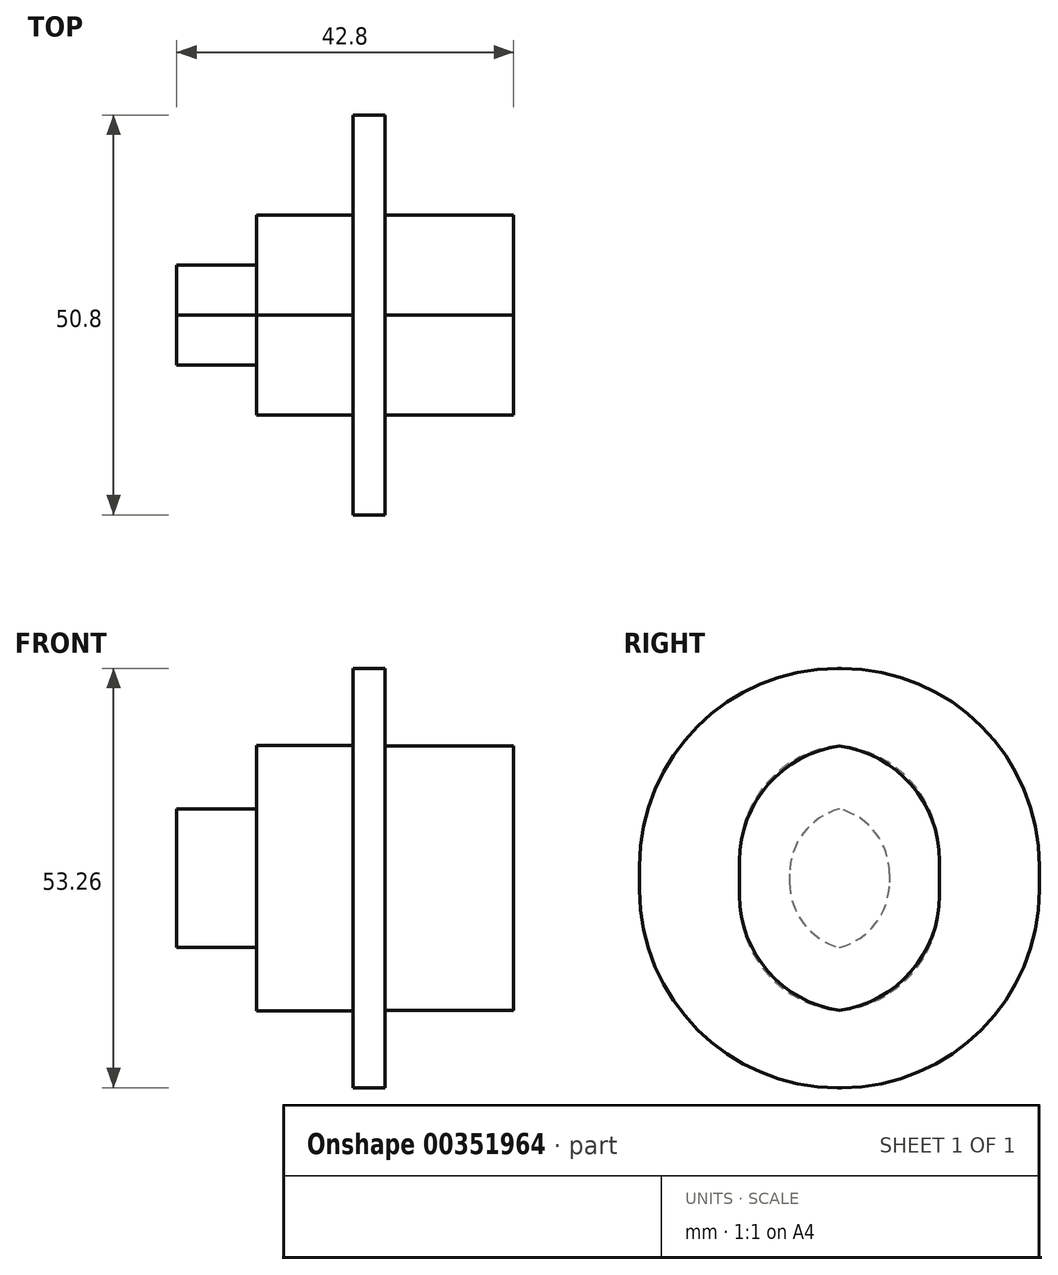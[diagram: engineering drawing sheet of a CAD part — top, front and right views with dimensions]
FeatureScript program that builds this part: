
annotation { "Feature Type Name" : "Feature", "Feature Type Description" : "" }
export const myFeature = defineFeature(function(context is Context, id is Id, definition is map)
    precondition{}
    {
        {
            var Q0;
            Q0=qCreatedBy(makeId("Front.planeOp"),FACE);
            var sketch = newSketch(context, id + "F0", { "sketchPlane" : qUnion([Q0])});
            skLineSegment(sketch, "E0.top", {"start": v(-32.63, 9.04) * mm, "end": v(-42.8, 9.04) * mm});
            skLineSegment(sketch, "E0.left", {"start": v(0, 0) * mm, "end": v(0, 9.04) * mm});
            skLineSegment(sketch, "E0.right", {"start": v(-42.8, 0) * mm, "end": v(-42.8, 9.04) * mm});
            skLineSegment(sketch, "E1.top", {"start": v(0, 16.87) * mm, "end": v(-16.32, 16.87) * mm});
            skLineSegment(sketch, "E1.left", {"start": v(0, 9.04) * mm, "end": v(0, 16.87) * mm});
            skLineSegment(sketch, "E1.right", {"start": v(-32.63, 9.04) * mm, "end": v(-32.63, 16.87) * mm});
            skLineSegment(sketch, "E2.top", {"start": v(-16.32, 26.6) * mm, "end": v(-20.42, 26.6) * mm});
            skLineSegment(sketch, "E2.left", {"start": v(-16.32, 16.87) * mm, "end": v(-16.32, 26.6) * mm});
            skLineSegment(sketch, "E2.right", {"start": v(-20.42, 16.87) * mm, "end": v(-20.42, 26.6) * mm});
            skLineSegment(sketch, "E3.trimOffspring", {"start": v(-20.42, 16.87) * mm, "end": v(-32.63, 16.87) * mm});
            skPoint(sketch, "E4.right.end.orphan", {"position": v(0, -9.18) * mm});
            skLineSegment(sketch, "E5.top", {"start": v(-42.8, -9.18) * mm, "end": v(-32.63, -9.18) * mm});
            skLineSegment(sketch, "E5.left", {"start": v(-42.8, 0) * mm, "end": v(-42.8, -9.18) * mm});
            skLineSegment(sketch, "E5.right", {"start": v(0, 0) * mm, "end": v(0, -9.18) * mm});
            skLineSegment(sketch, "E6.top", {"start": v(-32.63, -16.98) * mm, "end": v(-20.42, -16.98) * mm});
            skLineSegment(sketch, "E6.left", {"start": v(-32.63, -9.18) * mm, "end": v(-32.63, -16.98) * mm});
            skLineSegment(sketch, "E6.right", {"start": v(0, -9.18) * mm, "end": v(0, -16.98) * mm});
            skLineSegment(sketch, "E7.top", {"start": v(-20.42, -26.67) * mm, "end": v(-16.32, -26.67) * mm});
            skLineSegment(sketch, "E7.left", {"start": v(-20.42, -16.98) * mm, "end": v(-20.42, -26.67) * mm});
            skLineSegment(sketch, "E7.right", {"start": v(-16.32, -16.98) * mm, "end": v(-16.32, -26.67) * mm});
            skLineSegment(sketch, "E8.trimOffspring", {"start": v(-16.32, -16.98) * mm, "end": v(0, -16.98) * mm});
            skLineSegment(sketch, "E9", {"start": v(-20.42, 16.87) * mm, "end": v(-20.42, -16.98) * mm});
            skLineSegment(sketch, "E10", {"start": v(-16.32, -16.98) * mm, "end": v(-16.32, 16.87) * mm});
            skLineSegment(sketch, "E11", {"start": v(-32.63, 9.04) * mm, "end": v(-32.63, -9.18) * mm});
            skSolve(sketch);
        }
        {
            var Q0;
            Q0=makeQuery(id+"F0.imprint","IMPRINT",FACE,{"disambiguationData":[TD([[makeQuery(id+"F0.imprint","IMPRINT",EDGE,{"derivedFrom":sQuery(id+"F0.wireOp",EDGE,"E2.top")}),1.0]])]});
            extrude(context, id + "F1", {"entities" : qUnion([Q0]), "endBound" : BoundingType.SYMMETRIC, "oppositeDirection" : true, "depth" : 50.8 * mm});
        }
        {
            var Q0;
            Q0=makeQuery(id+"F0.imprint","IMPRINT",FACE,{"disambiguationData":[TD([[makeQuery(id+"F0.imprint","IMPRINT",EDGE,{"derivedFrom":sQuery(id+"F0.wireOp",EDGE,"E1.right")}),-1.0]])]});
            var Q1;
            Q1=makeQuery(id+"F0.imprint","IMPRINT",FACE,{"disambiguationData":[TD([[makeQuery(id+"F0.imprint","IMPRINT",EDGE,{"derivedFrom":sQuery(id+"F0.wireOp",EDGE,"E0.left")}),1.0]])]});
            extrude(context, id + "F2", {"entities" : qUnion([Q0, Q1]), "operationType" : NewBodyOperationType.ADD, "endBound" : BoundingType.SYMMETRIC, "depth" : 25.4 * mm});
        }
        {
            var Q0;
            Q0=makeQuery(id+"F0.imprint","IMPRINT",FACE,{"disambiguationData":[TD([[makeQuery(id+"F0.imprint","IMPRINT",EDGE,{"derivedFrom":sQuery(id+"F0.wireOp",EDGE,"E0.top")}),1.0]])]});
            extrude(context, id + "F3", {"entities" : qUnion([Q0]), "operationType" : NewBodyOperationType.ADD, "endBound" : BoundingType.SYMMETRIC, "depth" : 12.7 * mm});
        }
        {
            var Q0;
            Q0=makeQuery(id+"F3.opExtrude","CAP_EDGE",EDGE,{"disambiguationData":[OSD([sQuery(id+"F0.wireOp",EDGE,"E0.top")])],"isStart":false});
            var Q1;
            Q1=makeQuery(id+"F3.opExtrude","CAP_EDGE",EDGE,{"disambiguationData":[OSD([sQuery(id+"F0.wireOp",EDGE,"E5.top")])],"isStart":false});
            var Q2;
            Q2=makeQuery(id+"F3.opExtrude","CAP_EDGE",EDGE,{"disambiguationData":[OSD([sQuery(id+"F0.wireOp",EDGE,"E0.top")])],"isStart":true});
            var Q3;
            Q3=makeQuery(id+"F3.opExtrude","CAP_EDGE",EDGE,{"disambiguationData":[OSD([sQuery(id+"F0.wireOp",EDGE,"E5.top")])],"isStart":true});
            fillet(context, id + "F4", {"entities" : qUnion([Q0, Q1, Q2, Q3]), "radius" : 8.58 * mm, "tangentPropagation" : true, "allowEdgeOverflow" : false});
        }
        {
            var Q0;
            Q0=makeQuery(id+"F2.opExtrude","CAP_EDGE",EDGE,{"disambiguationData":[OSD([sQuery(id+"F0.wireOp",EDGE,"E3.trimOffspring")])],"isStart":true});
            var Q1;
            Q1=makeQuery(id+"F2.opExtrude","CAP_EDGE",EDGE,{"disambiguationData":[OSD([sQuery(id+"F0.wireOp",EDGE,"E6.top")])],"isStart":true});
            var Q2;
            Q2=makeQuery(id+"F2.opExtrude","CAP_EDGE",EDGE,{"disambiguationData":[OSD([sQuery(id+"F0.wireOp",EDGE,"E3.trimOffspring")])],"isStart":false});
            var Q3;
            Q3=makeQuery(id+"F2.opExtrude","CAP_EDGE",EDGE,{"disambiguationData":[OSD([sQuery(id+"F0.wireOp",EDGE,"E6.top")])],"isStart":false});
            fillet(context, id + "F5", {"entities" : qUnion([Q0, Q1, Q2, Q3]), "radius" : 14.1 * mm, "tangentPropagation" : true, "allowEdgeOverflow" : false});
        }
        {
            var Q0;
            Q0=makeQuery(id+"F1.opExtrude","CAP_EDGE",EDGE,{"disambiguationData":[OSD([sQuery(id+"F0.wireOp",EDGE,"E2.top")])],"isStart":true});
            var Q1;
            Q1=makeQuery(id+"F1.opExtrude","CAP_EDGE",EDGE,{"disambiguationData":[OSD([sQuery(id+"F0.wireOp",EDGE,"E7.top")])],"isStart":true});
            var Q2;
            Q2=makeQuery(id+"F1.opExtrude","CAP_EDGE",EDGE,{"disambiguationData":[OSD([sQuery(id+"F0.wireOp",EDGE,"E2.top")])],"isStart":false});
            var Q3;
            Q3=makeQuery(id+"F1.opExtrude","CAP_EDGE",EDGE,{"disambiguationData":[OSD([sQuery(id+"F0.wireOp",EDGE,"E7.top")])],"isStart":false});
            fillet(context, id + "F6", {"entities" : qUnion([Q0, Q1, Q2, Q3]), "radius" : 25.14 * mm, "tangentPropagation" : true, "allowEdgeOverflow" : false});
        }
        {
            var Q0;
            Q0=makeQuery(id+"F2.opExtrude","CAP_EDGE",EDGE,{"disambiguationData":[OSD([sQuery(id+"F0.wireOp",EDGE,"E1.top")])],"isStart":true});
            var Q1;
            Q1=makeQuery(id+"F2.opExtrude","CAP_EDGE",EDGE,{"disambiguationData":[OSD([sQuery(id+"F0.wireOp",EDGE,"E8.trimOffspring")])],"isStart":true});
            var Q2;
            Q2=makeQuery(id+"F2.opExtrude","CAP_EDGE",EDGE,{"disambiguationData":[OSD([sQuery(id+"F0.wireOp",EDGE,"E1.top")])],"isStart":false});
            var Q3;
            Q3=makeQuery(id+"F2.opExtrude","CAP_EDGE",EDGE,{"disambiguationData":[OSD([sQuery(id+"F0.wireOp",EDGE,"E8.trimOffspring")])],"isStart":false});
            fillet(context, id + "F7", {"entities" : qUnion([Q0, Q1, Q2, Q3]), "radius" : 14.72 * mm, "tangentPropagation" : true, "allowEdgeOverflow" : false});
        }
    });
